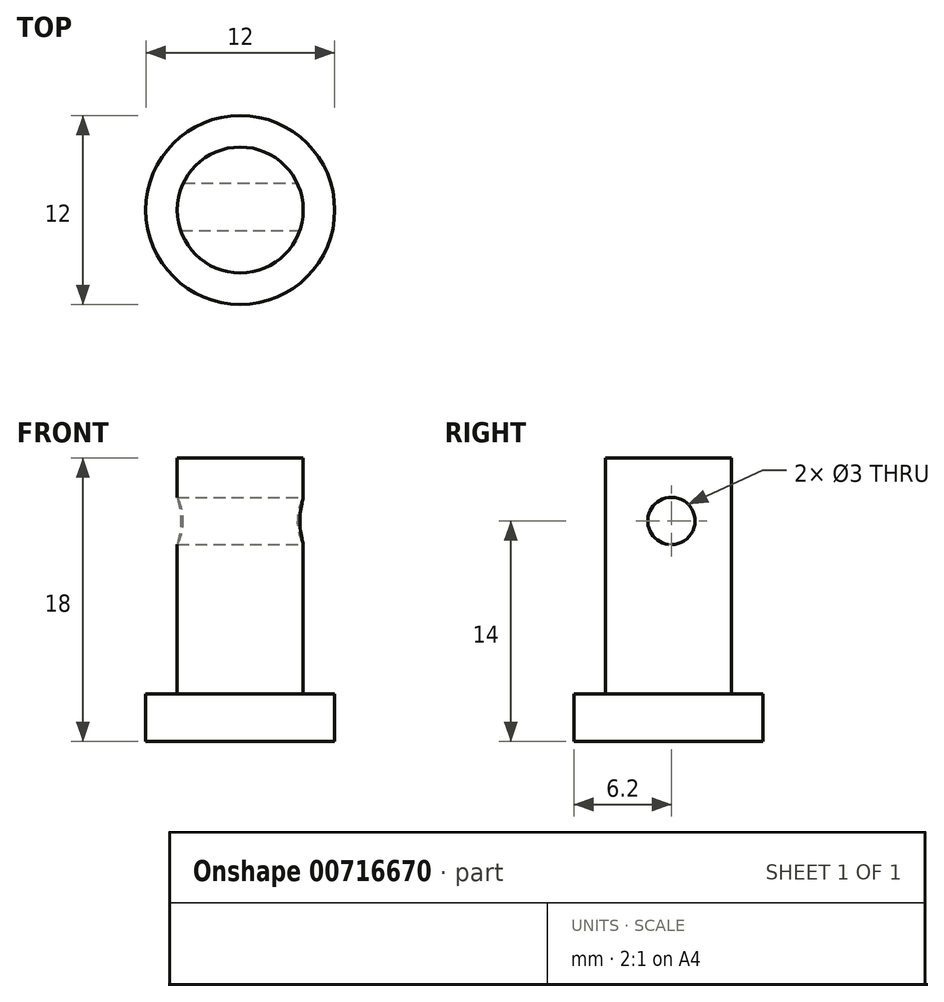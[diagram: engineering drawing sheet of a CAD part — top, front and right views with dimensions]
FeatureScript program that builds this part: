
annotation { "Feature Type Name" : "Feature", "Feature Type Description" : "" }
export const myFeature = defineFeature(function(context is Context, id is Id, definition is map)
    precondition{}
    {
        {
            var Q0;
            Q0=qCreatedBy(makeId("Top.planeOp"),FACE);
            var sketch = newSketch(context, id + "F0", { "sketchPlane" : qUnion([Q0])});
            skCircle(sketch, "E0", {"center": v(-10.27, 12.43) * mm, "radius": 6 * mm});
            skSolve(sketch);
        }
        {
            var Q0;
            Q0 = qSketchRegion(id + "F0", true);
            extrude(context, id + "F1", {"entities" : qUnion([Q0]), "depth" : 3 * mm, "offsetDistance" : 25.4 * mm});
        }
        {
            var Q0;
            Q0=makeQuery(id+"F1.opExtrude","CAP_FACE",FACE,{"disambiguationData":[OSD([sQuery(id+"F0.wireOp",EDGE,"E0")])],"isStart":false});
            var sketch = newSketch(context, id + "F2", { "sketchPlane" : qUnion([Q0])});
            skCircle(sketch, "E1", {"center": v(-10.27, 12.43) * mm, "radius": 4 * mm});
            skSolve(sketch);
        }
        {
            var Q0;
            Q0=makeQuery(id+"F2.imprint","IMPRINT",FACE,{"disambiguationData":[TD([[makeQuery(id+"F2.imprint","IMPRINT",EDGE,{"derivedFrom":sQuery(id+"F2.wireOp",EDGE,"E1")}),1.0]])]});
            var Q1;
            Q1=sQuery(id+"F2.wireOp",EDGE,"E1");
            extrude(context, id + "F3", {"entities" : qUnion([Q0]), "surfaceEntities" : qUnion([Q1]), "depth" : 15 * mm, "offsetDistance" : 25.4 * mm});
        }
        {
            var Q0;
            Q0=qCreatedBy(makeId("Right.planeOp"),FACE);
            var sketch = newSketch(context, id + "F4", { "sketchPlane" : qUnion([Q0])});
            skCircle(sketch, "E2", {"center": v(12.63, 14) * mm, "radius": 1.5 * mm});
            skSolve(sketch);
        }
        {
            var Q0;
            Q0=makeQuery(id+"F4.imprint","IMPRINT",FACE,{"disambiguationData":[TD([[makeQuery(id+"F4.imprint","IMPRINT",EDGE,{"derivedFrom":sQuery(id+"F4.wireOp",EDGE,"E2")}),1.0]])]});
            var Q1;
            Q1=sQuery(id+"F4.wireOp",EDGE,"E2");
            extrude(context, id + "F5", {"entities" : qUnion([Q0]), "operationType" : NewBodyOperationType.REMOVE, "surfaceEntities" : qUnion([Q1]), "oppositeDirection" : true, "depth" : 25.4 * mm, "offsetDistance" : 25.4 * mm});
        }
        {
            var Q0;
            Q0=makeQuery(id+"F3.opExtrude","SWEPT_BODY",BODY,{"disambiguationData":[OSD([sQuery(id+"F2.wireOp",EDGE,"E1")])]});
            transform(context, id + "F6", {"entities" : qUnion([Q0]), "transformType" : TransformType.TRANSLATION_3D, "dx" : 0 * mm, "dy" : 0 * mm, "dz" : 0 * mm, "makeCopy" : true});
        }
    });
